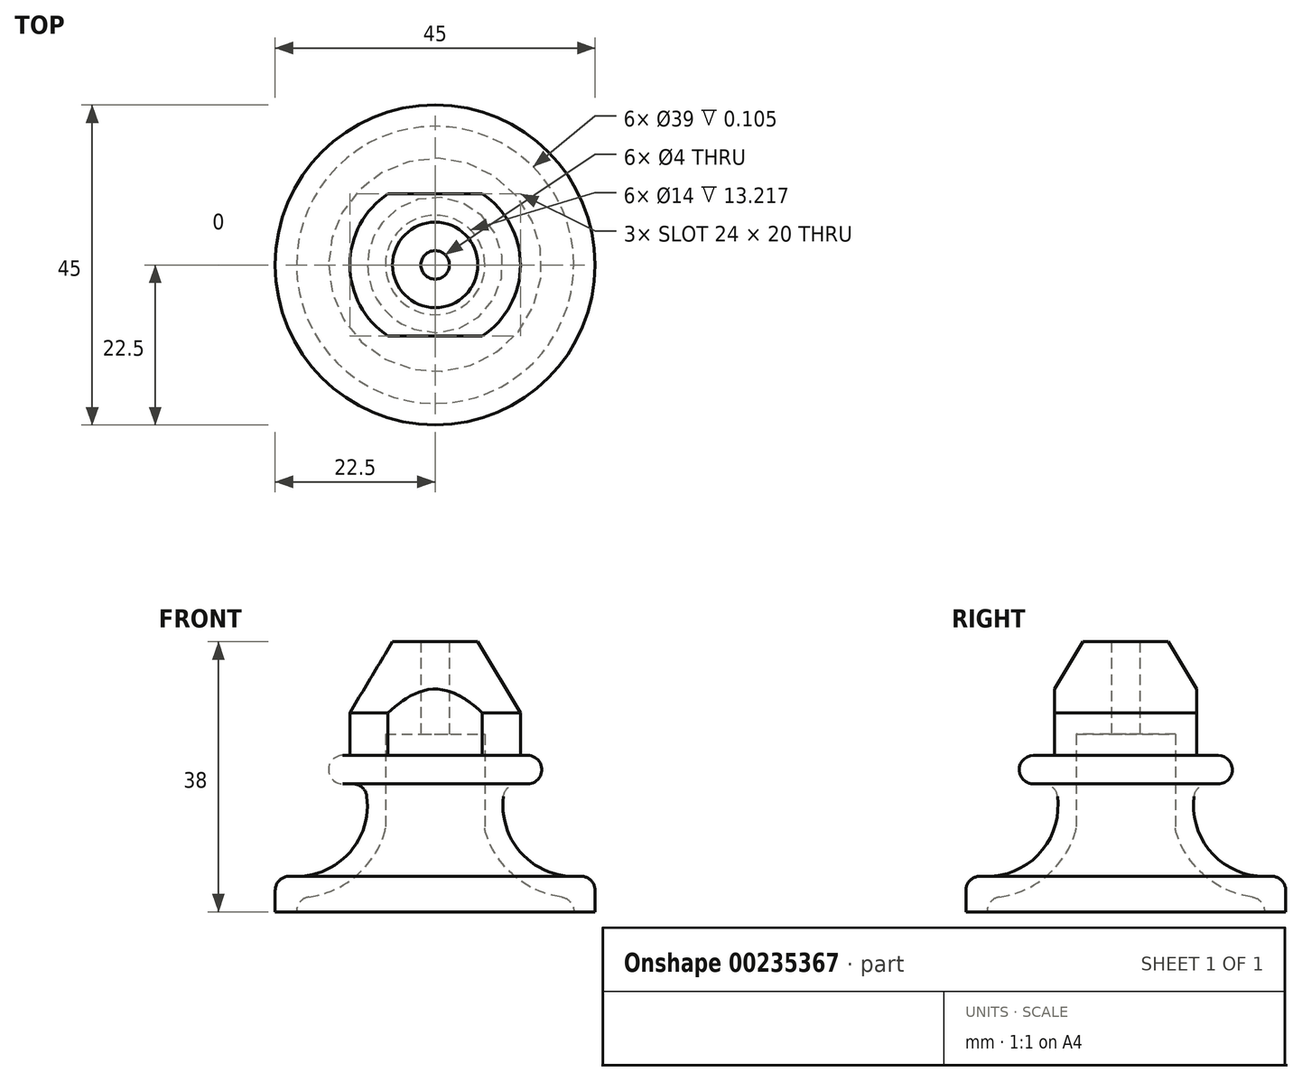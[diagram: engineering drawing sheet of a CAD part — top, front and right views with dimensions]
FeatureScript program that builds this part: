
annotation { "Feature Type Name" : "Feature", "Feature Type Description" : "" }
export const myFeature = defineFeature(function(context is Context, id is Id, definition is map)
    precondition{}
    {
        {
            var Q0;
            Q0=qCreatedBy(makeId("Front.planeOp"),FACE);
            var sketch = newSketch(context, id + "F0", { "sketchPlane" : qUnion([Q0])});
            skLineSegment(sketch, "E0", {"start": v(0, 0) * mm, "end": v(0, 42.42) * mm, "construction": true});
            skLineSegment(sketch, "E1", {"start": v(0, 0) * mm, "end": v(22.5, 0) * mm});
            skLineSegment(sketch, "E2", {"start": v(22.5, 0) * mm, "end": v(22.5, 3) * mm});
            skLineSegment(sketch, "E3", {"start": v(0, 38) * mm, "end": v(6, 38) * mm});
            skLineSegment(sketch, "E4", {"start": v(6, 38) * mm, "end": v(12, 28) * mm});
            skLineSegment(sketch, "E5", {"start": v(12, 28) * mm, "end": v(12, 22) * mm});
            skLineSegment(sketch, "E6", {"start": v(2, 38) * mm, "end": v(2, 25) * mm});
            skLineSegment(sketch, "E7", {"start": v(2, 25) * mm, "end": v(7, 25) * mm});
            skLineSegment(sketch, "E8", {"start": v(7, 25) * mm, "end": v(7, 11.78) * mm});
            skLineSegment(sketch, "E9", {"start": v(12, 22) * mm, "end": v(13, 22) * mm});
            skArc(sketch, "E10", {"start": v(13, 18) * mm, "mid": v(15, 20) * mm, "end": v(13, 22) * mm});
            skLineSegment(sketch, "E11", {"start": v(13, 18) * mm, "end": v(11.6, 18) * mm});
            skPoint(sketch, "E12.visualSharp", {"position": v(22.5, 7.09) * mm});
            skArc(sketch, "E12.filletArc", {"start": v(22.5, 3) * mm, "mid": v(21.86, 4.48) * mm, "end": v(20.34, 5) * mm});
            skArc(sketch, "E13", {"start": v(9.61, 16.26) * mm, "mid": v(12.29, 8.07) * mm, "end": v(20.34, 5) * mm});
            skPoint(sketch, "E14.visualSharp", {"position": v(10, 18) * mm});
            skArc(sketch, "E14.filletArc", {"start": v(11.6, 18) * mm, "mid": v(10.28, 17.5) * mm, "end": v(9.61, 16.26) * mm});
            skLineSegment(sketch, "E15", {"start": v(19.5, 0) * mm, "end": v(19.5, 0.1) * mm});
            skArc(sketch, "E16.0", {"start": v(7.09, 11.2) * mm, "mid": v(11.1, 5.08) * mm, "end": v(17.77, 2.09) * mm});
            skPoint(sketch, "E17.visualSharp", {"position": v(7, 11.5) * mm});
            skArc(sketch, "E17.filletArc", {"start": v(7, 11.78) * mm, "mid": v(7.02, 11.5) * mm, "end": v(7.09, 11.2) * mm});
            skPoint(sketch, "E18.visualSharp", {"position": v(19.5, 1.97) * mm});
            skArc(sketch, "E18.filletArc", {"start": v(19.5, 0.1) * mm, "mid": v(19, 1.42) * mm, "end": v(17.77, 2.09) * mm});
            skSolve(sketch);
        }
        {
            var Q0;
            {var subQ0=sQuery(id+"F0.wireOp",EDGE,"E2");Q0=makeQuery(id+"F0.imprint","IMPRINT",FACE,{"disambiguationData":[TD([[makeQuery(id+"F0.imprint","IMPRINT",EDGE,{"derivedFrom":subQ0}),1.0]])]});}
            var Q1;
            Q1=sQuery(id+"F0.wireOp",EDGE,"E0");
            revolve(context, id + "F1", {"entities" : qUnion([Q0]), "axis" : qUnion([Q1]), "revolveType" : RevolveType.FULL});
        }
        {
            var Q0;
            Q0=qCreatedBy(makeId("Right.planeOp"),FACE);
            var sketch = newSketch(context, id + "F2", { "sketchPlane" : qUnion([Q0])});
            skLineSegment(sketch, "E19", {"start": v(-12, 28) * mm, "end": v(-6, 38) * mm, "construction": true});
            skLineSegment(sketch, "E20", {"start": v(6, 38) * mm, "end": v(12, 28) * mm, "construction": true});
            skLineSegment(sketch, "E21", {"start": v(-12, 22) * mm, "end": v(-12, 28) * mm, "construction": true});
            skLineSegment(sketch, "E22", {"start": v(12, 28) * mm, "end": v(12, 22) * mm, "construction": true});
            skLineSegment(sketch, "E23", {"start": v(-12, 22) * mm, "end": v(12, 22) * mm, "construction": true});
            skLineSegment(sketch, "E24.bottom", {"start": v(-10, 22) * mm, "end": v(-23.47, 22) * mm});
            skLineSegment(sketch, "E24.top", {"start": v(-10, 36.71) * mm, "end": v(-23.47, 36.71) * mm});
            skLineSegment(sketch, "E24.left", {"start": v(-10, 22) * mm, "end": v(-10, 36.71) * mm});
            skLineSegment(sketch, "E24.right", {"start": v(-23.47, 22) * mm, "end": v(-23.47, 36.71) * mm});
            skLineSegment(sketch, "E25.bottom", {"start": v(10, 22) * mm, "end": v(18.1, 22) * mm});
            skLineSegment(sketch, "E25.top", {"start": v(10, 36.33) * mm, "end": v(18.1, 36.33) * mm});
            skLineSegment(sketch, "E25.left", {"start": v(10, 22) * mm, "end": v(10, 36.33) * mm});
            skLineSegment(sketch, "E25.right", {"start": v(18.1, 22) * mm, "end": v(18.1, 36.33) * mm});
            skSolve(sketch);
        }
        {
            var Q0;
            Q0 = qSketchRegion(id + "F2", true);
            extrude(context, id + "F3", {"entities" : qUnion([Q0]), "operationType" : NewBodyOperationType.REMOVE, "endBound" : BoundingType.THROUGH_ALL, "oppositeDirection" : true, "depth" : 25 * mm, "hasSecondDirection" : true, "secondDirectionBound" : SecondDirectionBoundingType.THROUGH_ALL, "secondDirectionOppositeDirection" : false, "secondDirectionDepth" : 25 * mm});
        }
    });
